# Revit family: PRE050018-FR
name_source: partatom
category: Accessoire de canalisation
revit_build: Autodesk Revit 2017 (Build: 20160225_1515(x64)
units: mm (PartAtom-declared; Revit-internal decimal feet)

## family parameters
Basée sur le plan de construction = Non
Cote de connecteur circulaire = Utiliser le diamètre
Couper avec des vides une fois chargée = Non
Partagée = Non
Toujours verticalement = Oui
Type d'élément = Normal

## types (4) — shared parameters
Adresse = 7, RUE RACINE - 92542 MONTROUGE CEDEX FRANCE
Debit = 8 l/min par limiteur de débit intégré

Brise-jet laminaire

Dispositif anti-coup de bélier
Diamètre Nominal = 12 mm  [stored 0.0393701 ft]
Fabricant = LES ROBINETS PRESTO S.A.
Flux = 0.1 L/s
Garantie = 3
Hauteur = 256 mm  [stored 0.839895 ft]
LC = 20 mm  [stored 0.0656168 ft]
Largeur = 60 mm  [stored 0.19685 ft]
Lien CCTP = http://www.prestodatashare.com
Lien fiche produit = http://www.prestodatashare.com
Lien notice d'utilisation = http://www.prestodatashare.com
Matériau = Laiton poli chromé
PC = 30 mm  [stored 0.0984252 ft]
Perte de charge = 0.0 Pa
Pression = 1 à 5 bars
Profondeur = 240 mm  [stored 0.787402 ft]
Raccordement = G 3/8'' (12x17)
URL = http://www.prestodatashare.com
URL Fabricant = http://www.prestodatashare.com
Variantes = 55130-55131-55135-55136

## per-type parameters (varying)
| type | Description | Finition | Fonction | Polantis code | Reference |
| 55136 PRESTO MITIGEUR PRESTO 5750 BEC STANDARD FIXE -SECTEUR | Mitigeur à détection (CE) sur plage avec sélecteur de température latérale. De type Presto 5750 réf. 55136 ou techniquement équivalent. Avec  bec fixe de hauteur standard. Une cellule optoélectronique, alimentation secteur (transformateur 230/7 Volt déporté dans boîtier étanche IP65). Limitation de la température maximale par butée réglable, régulateur de débit intégré (3 l/min). Système antiblocage interdisant l'écoulement en continu. Avec flexibles PEX et robinets d’arrêt filtres. | Corps en laiton chromé

Bec standard fixe en laiton chromé | Pression d'utilisation recommandée :
- 1 à 5 bars

Débit :
- 8 l/mn par limiteur de débit intégré
- Brise-jet laminaire
- Dispositif anti-coup de bélier

Alimentation hydraulique :
- G 3/8'' (12x17)

Alimentation électrique :
- Transformateur 230 / 7 Volts dans boîtier déporté étanche IP65

Matière et couleur de finition :
- Corps en laiton chromé
- Bec standard fixe en laiton chromé

Résistance thermique :
- Résiste à une température de 75°C durant 30 minutes dans le cadre de chocs thermiques

Sécurité :
- Fermeture automatique de l'électrovanne en cas d'écoulement > à 30s ou de dégradation du détecteur
- Ecoulement automatique de 30 secondes, 72 heures après la dernière utilisation

Livré avec :
- 1 Ecrou de fixation
- 1 Joint et rondelle
- 2 Flexibles PEX avec écrou femelle 3/8'' (12x17) avec Clapets anti-retour NF
- 2 Robinets d'arrêts filtres et rosaces pour le montage applique équerre
- 1 Autocollant de signalisation

Normes / Agréments :
- Laiton conforme aux normes NF EN1982, EN12164, NF EN12165
- Résistant au brouillard salin 200 H (essai NSS) conformément à la norme NF ISO 9227 | PRE050018c-FR | 55136 |
| 55135 PRESTO MITIGEUR PRESTO 5750 BEC STANDARD EMBASE TOURNANTE - SECTEUR | Mitigeur à détection (CE) sur plage avec sélecteur de température latérale. De type Presto 5750 réf. 55135 ou techniquement équivalent. Avec  bec tournant de hauteur standard. Une cellule optoélectronique, alimentation secteur (transformateur 230/7 Volt déporté dans boîtier étanche IP65). Limitation de la température maximale par butée réglable, régulateur de débit intégré (3 l/min). Système antiblocage interdisant l'écoulement en continu. Avec flexibles PEX et robinets d’arrêt filtres. | Corps en laiton chromé

Bec standard mobile en laiton chromé | Pression d'utilisation recommandée :
- 1 à 5 bars

Débit :
- 8 l/mn par limiteur de débit intégré
- Brise-jet laminaire
- Dispositif anti-coup de bélier

Alimentation hydraulique :
- G 3/8'' (12x17)

Alimentation électrique :
- Transformateur 230 / 7 Volts dans boîtier déporté étanche IP65

Matière et couleur de finition :
- Corps en laiton chromé
- Bec standard - embase tournante en laiton chromé

Résistance thermique :
- Résiste à une température de 75°C durant 30 minutes dans le cadre de chocs thermiques

Sécurité :
- Fermeture automatique de l'électrovanne en cas d'écoulement > à 30s ou de dégradation du détecteur
- Ecoulement automatique de 30 secondes, 72 heures après la dernière utilisation

Livré avec :
- 1 Ecrou de fixation
- 1 Joint et rondelle
- 2 Flexibles PEX avec écrou femelle 3/8'' (12x17) avec Clapets anti-retour NF
- 2 Robinets d'arrêts filtres et rosaces pour le montage applique équerre
- 1 Autocollant de signalisation

Normes / Agréments :
- Laiton conforme aux normes NF EN1982, EN12164, NF EN12165
- Résistant au brouillard salin 200 H (essai NSS) conformément à la norme NF ISO 9227 | PRE050018b-FR | 55135 |
| 55131 PRESTO MITIGEUR PRESTO 5750 BEC STANDARD FIXE -PILE | Mitigeur à détection (CE) sur plage avec sélecteur de température latérale. De type Presto 5750 réf. 55131 ou techniquement équivalent. Avec  bec fixe de hauteur standard. Une cellule optoélectronique, une alimentation par pile lithium 6 V intégrée dans le robinet. Limitation de la température maximale par butée réglable, régulateur de débit intégré (8l/min). Système antiblocage interdisant l'écoulement en continu. Avec flexibles PEX et robinets d’arrêt filtres. | Corps en laiton chromé

Bec standard fixe en laiton chromé | Pression d'utilisation recommandée :
- 1 à 5 bars

Débit :
- 8 l/mn par limiteur de débit intégré
- Brise-jet laminaire
- Dispositif anti-coup de bélier

Alimentation hydraulique :
- G 3/8'' (12x17)

Alimentation électrique :
- Pile lithium 6 volts type CRP2 dans boîtier déporté

Matière et couleur de finition :
- Corps en laiton chromé
- Bec standard fixe en laiton chromé

Résistance thermique :
- Résiste à une température de 75°C durant 30 minutes dans le cadre de chocs thermiques

Sécurité :
- Fermeture automatique de l'électrovanne en cas d'écoulement > à 30s, d'usure de la pile ou de dégradation du détecteur
- Ecoulement automatique de 30 secondes, 72 heures après la dernière utilisation

Livré avec :
- 1 Ecrou de fixation
- 1 Joint et rondelle
- 2 Flexibles PEX avec écrou femelle 3/8'' (12x17) avec Clapets
  anti-retour NF
- 2 Robinets d'arrêts filtres et rosaces pour le montage applique équerre
- 1 Autocollant de signalisation

Normes / Agréments :
- Laiton conforme aux normes NF EN1982, EN12164, NF EN12165
- Résistant au brouillard salin 200 H (essai NSS) conformément à la norme NF ISO 9227 | PRE050018a-FR | 55131 |
| 55130 PRESTO MITIGEUR PRESTO 5750 BEC STANDARD EMBASE TOURNANTE - PILE | Mitigeur à détection (CE) sur plage avec sélecteur de température latérale. De type Presto 5750 réf. 55130 ou techniquement équivalent. Avec  bec tournant de hauteur standard. Une cellule optoélectronique, une alimentation par pile lithium 6 V intégrée dans le robinet. Limitation de la température maximale par butée réglable, régulateur de débit intégré (8 l/min). Système antiblocage interdisant l'écoulement en continu. Avec flexibles PEX et robinets d’arrêt filtres. | Corps en laiton chromé

Bec standard tournant en laiton chromé | Pression d'utilisation recommandée :
- 1 à 5 bars

Débit :
- 8 l/mn par limiteur de débit intégré
- Brise-jet laminaire
- Dispositif anti-coup de bélier

Alimentation hydraulique :
- G 3/8'' (12x17)

Alimentation électrique :
- Pile lithium 6 volts type CRP2 dans boîtier déporté

Matière et couleur de finition :
- Corps en laiton chromé
- Bec standard - embase tournante en laiton chromé

Résistance thermique :
- Résiste à une température de 75°C durant 30 minutes dans le cadre de chocs thermiques

Sécurité :
- Fermeture automatique de l'électrovanne en cas d'écoulement > à 30s, d'usure de la pile ou de dégradation du détecteur
- Ecoulement automatique de 30 secondes, 72 heures après la dernière utilisation

Livré avec :
- 1 Ecrou de fixation
- 1 Joint et rondelle
- 2 Flexibles PEX avec écrou femelle 3/8'' (12x17) avec Clapets anti-retour NF
- 2 Robinets d'arrêts filtres et rosaces pour le montage applique équerre
- 1 Autocollant de signalisation

Normes / Agréments :
- Laiton conforme aux normes NF EN1982, EN12164, NF EN12165
- Résistant au brouillard salin 200 H (essai NSS) conformément à la norme NF ISO 9227 | PRE050018-FR | 55130 |

note: column(s) folded — value = type name in every type: Modèle

note: [stored X ft] marks values corroborated as IEEE doubles in the binary element streams (Revit-internal decimal feet)
